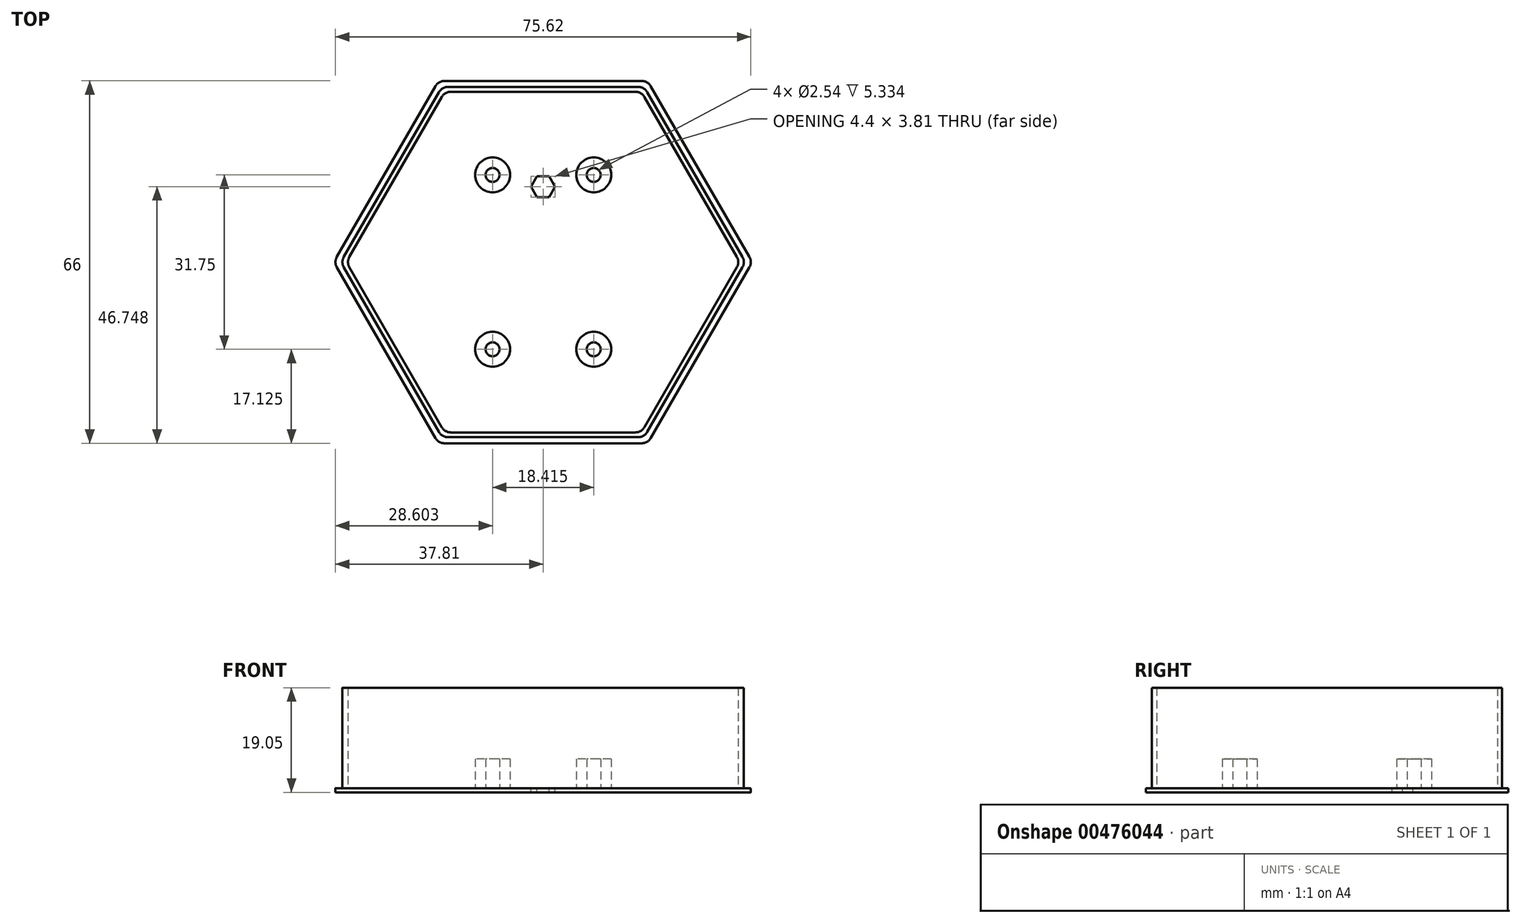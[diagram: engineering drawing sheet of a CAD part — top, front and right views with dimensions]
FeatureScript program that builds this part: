
annotation { "Feature Type Name" : "Feature", "Feature Type Description" : "" }
export const myFeature = defineFeature(function(context is Context, id is Id, definition is map)
    precondition{}
    {
        {
            var Q0;
            Q0=qCreatedBy(makeId("Top.planeOp"),FACE);
            var sketch = newSketch(context, id + "F0", { "sketchPlane" : qUnion([Q0])});
            skLineSegment(sketch, "E0", {"start": v(-56.1, -68.55) * mm, "end": v(58.07, -68.55) * mm});
            skLineSegment(sketch, "E1", {"start": v(0, 0) * mm, "end": v(-19.05, 33) * mm, "construction": true});
            skLineSegment(sketch, "E2", {"start": v(19.05, 33) * mm, "end": v(0, 0) * mm, "construction": true});
            skLineSegment(sketch, "E3", {"start": v(-19.05, 33) * mm, "end": v(19.05, 33) * mm});
            skLineSegment(sketch, "E4.1.0", {"start": v(-38.1, 0) * mm, "end": v(-19.05, 33) * mm});
            skLineSegment(sketch, "E4.2.0", {"start": v(-19.05, -33) * mm, "end": v(-38.1, 0) * mm});
            skLineSegment(sketch, "E4.3.0", {"start": v(19.05, -33) * mm, "end": v(-19.05, -33) * mm});
            skLineSegment(sketch, "E4.4.0", {"start": v(38.1, 0) * mm, "end": v(19.05, -33) * mm});
            skLineSegment(sketch, "E4.5.0", {"start": v(19.05, 33) * mm, "end": v(38.1, 0) * mm});
            skPoint(sketch, "E4.center", {"position": v(0, 0) * mm});
            skSolve(sketch);
        }
        {
            var Q0;
            Q0=makeQuery(id+"F0.imprint","IMPRINT",FACE,{"disambiguationData":[TD([[makeQuery(id+"F0.imprint","IMPRINT",EDGE,{"derivedFrom":sQuery(id+"F0.wireOp",EDGE,"E3")}),-1.0]])]});
            extrude(context, id + "F1", {"entities" : qUnion([Q0]), "depth" : 0.76 * mm, "offsetDistance" : 25.4 * mm});
        }
        {
            var Q0;
            Q0=makeQuery(id+"FdZoSmRdGPEDfu0_1.splitOp","SPLIT",EDGE,{"derivedFrom":makeQuery(id+"F1.opExtrude","SWEPT_EDGE",EDGE,{"disambiguationData":[OSD([sQuery(id+"F0.wireOp",EDGE,"E4.4.0"),sQuery(id+"F0.wireOp",EDGE,"E4.5.0")])]})});
            var Q1;
            Q1=makeQuery(id+"FdZoSmRdGPEDfu0_1.splitOp","SPLIT",EDGE,{"derivedFrom":makeQuery(id+"F1.opExtrude","SWEPT_EDGE",EDGE,{"disambiguationData":[OSD([sQuery(id+"F0.wireOp",EDGE,"E3"),sQuery(id+"F0.wireOp",EDGE,"E4.5.0")])]})});
            var Q2;
            Q2=makeQuery(id+"FdZoSmRdGPEDfu0_1.splitOp","SPLIT",EDGE,{"derivedFrom":makeQuery(id+"F1.opExtrude","SWEPT_EDGE",EDGE,{"disambiguationData":[OSD([sQuery(id+"F0.wireOp",EDGE,"E3"),sQuery(id+"F0.wireOp",EDGE,"E4.1.0")])]})});
            var Q3;
            Q3=makeQuery(id+"FdZoSmRdGPEDfu0_1.splitOp","SPLIT",EDGE,{"derivedFrom":makeQuery(id+"F1.opExtrude","SWEPT_EDGE",EDGE,{"disambiguationData":[OSD([sQuery(id+"F0.wireOp",EDGE,"E4.1.0"),sQuery(id+"F0.wireOp",EDGE,"E4.2.0")])]})});
            var Q4;
            Q4=makeQuery(id+"FdZoSmRdGPEDfu0_1.splitOp","SPLIT",EDGE,{"derivedFrom":makeQuery(id+"F1.opExtrude","SWEPT_EDGE",EDGE,{"disambiguationData":[OSD([sQuery(id+"F0.wireOp",EDGE,"E4.2.0"),sQuery(id+"F0.wireOp",EDGE,"E4.3.0")])]})});
            var Q5;
            Q5=makeQuery(id+"FdZoSmRdGPEDfu0_1.splitOp","SPLIT",EDGE,{"derivedFrom":makeQuery(id+"F1.opExtrude","SWEPT_EDGE",EDGE,{"disambiguationData":[OSD([sQuery(id+"F0.wireOp",EDGE,"E4.3.0"),sQuery(id+"F0.wireOp",EDGE,"E4.4.0")])]})});
            fillet(context, id + "F2", {"entities" : qUnion([Q0, Q1, Q2, Q3, Q4, Q5]), "radius" : 1.9 * mm, "allowEdgeOverflow" : false});
        }
        {
            var Q0;
            Q0=qCreatedBy(makeId("Top.planeOp"),FACE);
            var sketch = newSketch(context, id + "F3", { "sketchPlane" : qUnion([Q0])});
            skLineSegment(sketch, "E5", {"start": v(0, 0) * mm, "end": v(-18.41, 31.9) * mm, "construction": true});
            skLineSegment(sketch, "E6", {"start": v(0, 0) * mm, "end": v(18.41, 31.9) * mm, "construction": true});
            skLineSegment(sketch, "E7", {"start": v(-18.41, 31.9) * mm, "end": v(18.41, 31.9) * mm});
            skLineSegment(sketch, "E8.1.0", {"start": v(-36.83, 0) * mm, "end": v(-18.41, 31.9) * mm});
            skLineSegment(sketch, "E8.2.0", {"start": v(-18.42, -31.9) * mm, "end": v(-36.83, 0) * mm});
            skLineSegment(sketch, "E8.3.0", {"start": v(18.41, -31.9) * mm, "end": v(-18.41, -31.9) * mm});
            skLineSegment(sketch, "E8.4.0", {"start": v(36.83, 0) * mm, "end": v(18.41, -31.9) * mm});
            skLineSegment(sketch, "E8.5.0", {"start": v(18.41, 31.9) * mm, "end": v(36.83, 0) * mm});
            skPoint(sketch, "E8.center", {"position": v(0, 0) * mm});
            skSolve(sketch);
        }
        {
            var Q0;
            Q0=qSketchRegion(id+"F3",true);
            extrude(context, id + "F4", {"entities" : qUnion([Q0]), "depth" : 19.05 * mm, "offsetDistance" : 25.4 * mm});
        }
        {
            var Q0;
            Q0=makeQuery(id+"F4.opExtrude","SWEPT_EDGE",EDGE,{"disambiguationData":[OSD([sQuery(id+"F3.wireOp",EDGE,"E8.2.0"),sQuery(id+"F3.wireOp",EDGE,"E8.3.0")])]});
            var Q1;
            Q1=makeQuery(id+"F4.opExtrude","SWEPT_EDGE",EDGE,{"disambiguationData":[OSD([sQuery(id+"F3.wireOp",EDGE,"E8.3.0"),sQuery(id+"F3.wireOp",EDGE,"E8.4.0")])]});
            var Q2;
            Q2=makeQuery(id+"F4.opExtrude","SWEPT_EDGE",EDGE,{"disambiguationData":[OSD([sQuery(id+"F3.wireOp",EDGE,"E8.4.0"),sQuery(id+"F3.wireOp",EDGE,"E8.5.0")])]});
            var Q3;
            Q3=makeQuery(id+"F4.opExtrude","SWEPT_EDGE",EDGE,{"disambiguationData":[OSD([sQuery(id+"F3.wireOp",EDGE,"E8.1.0"),sQuery(id+"F3.wireOp",EDGE,"E8.2.0")])]});
            var Q4;
            Q4=makeQuery(id+"F4.opExtrude","SWEPT_EDGE",EDGE,{"disambiguationData":[OSD([sQuery(id+"F3.wireOp",EDGE,"E7"),sQuery(id+"F3.wireOp",EDGE,"E8.5.0")])]});
            var Q5;
            Q5=makeQuery(id+"F4.opExtrude","SWEPT_EDGE",EDGE,{"disambiguationData":[OSD([sQuery(id+"F3.wireOp",EDGE,"E7"),sQuery(id+"F3.wireOp",EDGE,"E8.1.0")])]});
            fillet(context, id + "F5", {"entities" : qUnion([Q0, Q1, Q2, Q3, Q4, Q5]), "radius" : 1.9 * mm, "tangentPropagation" : true, "allowEdgeOverflow" : false});
        }
        {
            var Q0;
            Q0=qCreatedBy(makeId("Top.planeOp"),FACE);
            var sketch = newSketch(context, id + "F6", { "sketchPlane" : qUnion([Q0])});
            skLineSegment(sketch, "E9", {"start": v(-17.9, 31.02) * mm, "end": v(0, 0) * mm, "construction": true});
            skLineSegment(sketch, "E10", {"start": v(0, 0) * mm, "end": v(17.9, 31.02) * mm, "construction": true});
            skLineSegment(sketch, "E11", {"start": v(-17.9, 31.02) * mm, "end": v(17.9, 31.02) * mm});
            skLineSegment(sketch, "E12.1.0", {"start": v(-35.81, 0) * mm, "end": v(-17.9, 31.02) * mm});
            skLineSegment(sketch, "E12.2.0", {"start": v(-17.9, -31.02) * mm, "end": v(-35.81, 0) * mm});
            skLineSegment(sketch, "E12.3.0", {"start": v(17.9, -31.02) * mm, "end": v(-17.9, -31.02) * mm});
            skLineSegment(sketch, "E12.4.0", {"start": v(35.81, 0) * mm, "end": v(17.9, -31.02) * mm});
            skLineSegment(sketch, "E12.5.0", {"start": v(17.9, 31.02) * mm, "end": v(35.81, 0) * mm});
            skPoint(sketch, "E12.center", {"position": v(0, 0) * mm});
            skSolve(sketch);
        }
        {
            var Q0;
            Q0 = qSketchRegion(id + "F6", true);
            extrude(context, id + "F7", {"entities" : qUnion([Q0]), "depth" : 25.4 * mm, "offsetDistance" : 25.4 * mm});
        }
        {
            var Q0;
            Q0=makeQuery(id+"F7.opExtrude","SWEPT_EDGE",EDGE,{"disambiguationData":[OSD([sQuery(id+"F6.wireOp",EDGE,"E12.2.0"),sQuery(id+"F6.wireOp",EDGE,"E12.3.0")])]});
            var Q1;
            Q1=makeQuery(id+"F7.opExtrude","SWEPT_EDGE",EDGE,{"disambiguationData":[OSD([sQuery(id+"F6.wireOp",EDGE,"E12.3.0"),sQuery(id+"F6.wireOp",EDGE,"E12.4.0")])]});
            var Q2;
            Q2=makeQuery(id+"F7.opExtrude","SWEPT_EDGE",EDGE,{"disambiguationData":[OSD([sQuery(id+"F6.wireOp",EDGE,"E12.4.0"),sQuery(id+"F6.wireOp",EDGE,"E12.5.0")])]});
            var Q3;
            Q3=makeQuery(id+"F7.opExtrude","SWEPT_EDGE",EDGE,{"disambiguationData":[OSD([sQuery(id+"F6.wireOp",EDGE,"E12.1.0"),sQuery(id+"F6.wireOp",EDGE,"E12.2.0")])]});
            var Q4;
            Q4=makeQuery(id+"F7.opExtrude","SWEPT_EDGE",EDGE,{"disambiguationData":[OSD([sQuery(id+"F6.wireOp",EDGE,"E11"),sQuery(id+"F6.wireOp",EDGE,"E12.5.0")])]});
            var Q5;
            Q5=makeQuery(id+"F7.opExtrude","SWEPT_EDGE",EDGE,{"disambiguationData":[OSD([sQuery(id+"F6.wireOp",EDGE,"E11"),sQuery(id+"F6.wireOp",EDGE,"E12.1.0")])]});
            fillet(context, id + "F8", {"entities" : qUnion([Q0, Q1, Q2, Q3, Q4, Q5]), "radius" : 1.9 * mm, "tangentPropagation" : true, "allowEdgeOverflow" : false});
        }
        {
            var Q0;
            Q0=makeQuery(id+"F7.opExtrude","SWEPT_BODY",BODY,{"disambiguationData":[OSD([sQuery(id+"F6.wireOp",EDGE,"E11"),sQuery(id+"F6.wireOp",EDGE,"E12.1.0"),sQuery(id+"F6.wireOp",EDGE,"E12.2.0"),sQuery(id+"F6.wireOp",EDGE,"E12.3.0"),sQuery(id+"F6.wireOp",EDGE,"E12.4.0"),sQuery(id+"F6.wireOp",EDGE,"E12.5.0")])]});
            transform(context, id + "F9", {"entities" : qUnion([Q0]), "transformType" : TransformType.TRANSLATION_3D, "dx" : 0 * mm, "dy" : 0 * mm, "dz" : 0.76 * mm, "makeCopy" : false});
        }
        {
            var Q0;
            Q0=makeQuery(id+"F7.opExtrude","SWEPT_BODY",BODY,{"disambiguationData":[OSD([sQuery(id+"F6.wireOp",EDGE,"E11"),sQuery(id+"F6.wireOp",EDGE,"E12.1.0"),sQuery(id+"F6.wireOp",EDGE,"E12.2.0"),sQuery(id+"F6.wireOp",EDGE,"E12.3.0"),sQuery(id+"F6.wireOp",EDGE,"E12.4.0"),sQuery(id+"F6.wireOp",EDGE,"E12.5.0")])]});
            var Q1;
            Q1=makeQuery(id+"F4.opExtrude","SWEPT_BODY",BODY,{"disambiguationData":[OSD([sQuery(id+"F3.wireOp",EDGE,"E7"),sQuery(id+"F3.wireOp",EDGE,"E8.1.0"),sQuery(id+"F3.wireOp",EDGE,"E8.2.0"),sQuery(id+"F3.wireOp",EDGE,"E8.3.0"),sQuery(id+"F3.wireOp",EDGE,"E8.4.0"),sQuery(id+"F3.wireOp",EDGE,"E8.5.0")])]});
            booleanBodies(context, id + "F10", {"operationType" : BooleanOperationType.SUBTRACTION, "tools" : qUnion([Q0]), "targets" : qUnion([Q1])});
        }
        {
            var Q0;
            Q0=makeQuery(id+"F10.opBoolean","COPY",FACE,{"derivedFrom":makeQuery(id+"F7.opExtrude","CAP_FACE",FACE,{"disambiguationData":[OSD([sQuery(id+"F6.wireOp",EDGE,"E11"),sQuery(id+"F6.wireOp",EDGE,"E12.1.0"),sQuery(id+"F6.wireOp",EDGE,"E12.2.0"),sQuery(id+"F6.wireOp",EDGE,"E12.3.0"),sQuery(id+"F6.wireOp",EDGE,"E12.4.0"),sQuery(id+"F6.wireOp",EDGE,"E12.5.0")])],"isStart":true})});
            var sketch = newSketch(context, id + "F11", { "sketchPlane" : qUnion([Q0])});
            skLineSegment(sketch, "E13.bottom", {"start": v(-12.7, 19.3) * mm, "end": v(12.7, 19.3) * mm});
            skLineSegment(sketch, "E13.top", {"start": v(-12.7, -19.3) * mm, "end": v(12.7, -19.3) * mm});
            skLineSegment(sketch, "E13.left", {"start": v(-12.7, 19.3) * mm, "end": v(-12.7, -19.3) * mm});
            skLineSegment(sketch, "E13.right", {"start": v(12.7, 19.3) * mm, "end": v(12.7, -19.3) * mm});
            skPoint(sketch, "E14", {"position": v(0, 13.75) * mm});
            skLineSegment(sketch, "E15", {"start": v(-12.7, 0) * mm, "end": v(12.7, 0) * mm, "construction": true});
            skLineSegment(sketch, "E16.bottom", {"start": v(9.2, 15.88) * mm, "end": v(-9.2, 15.88) * mm, "construction": true});
            skLineSegment(sketch, "E16.top", {"start": v(9.2, -15.88) * mm, "end": v(-9.2, -15.88) * mm, "construction": true});
            skLineSegment(sketch, "E16.left", {"start": v(9.2, 15.87) * mm, "end": v(9.2, -15.88) * mm, "construction": true});
            skLineSegment(sketch, "E16.right", {"start": v(-9.2, 15.88) * mm, "end": v(-9.2, -15.88) * mm, "construction": true});
            skCircle(sketch, "E17", {"center": v(-9.2, 15.88) * mm, "radius": 3.18 * mm});
            skCircle(sketch, "E18", {"center": v(9.2, 15.88) * mm, "radius": 3.18 * mm});
            skCircle(sketch, "E19", {"center": v(-9.2, -15.88) * mm, "radius": 3.18 * mm});
            skCircle(sketch, "E20", {"center": v(9.2, -15.88) * mm, "radius": 3.18 * mm});
            skCircle(sketch, "E21", {"center": v(-9.2, 15.88) * mm, "radius": 1.27 * mm});
            skCircle(sketch, "E22", {"center": v(9.2, 15.88) * mm, "radius": 1.27 * mm});
            skCircle(sketch, "E23", {"center": v(-9.2, -15.88) * mm, "radius": 1.27 * mm});
            skCircle(sketch, "E24", {"center": v(9.2, -15.88) * mm, "radius": 1.27 * mm});
            skCircle(sketch, "E25.cCircle", {"center": v(0, 13.75) * mm, "radius": 1.9 * mm, "construction": true});
            skLineSegment(sketch, "E25.0", {"start": v(1.1, 11.84) * mm, "end": v(-1.1, 11.84) * mm});
            skLineSegment(sketch, "E25.1", {"start": v(-1.1, 11.84) * mm, "end": v(-2.2, 13.75) * mm});
            skLineSegment(sketch, "E25.2", {"start": v(-2.2, 13.75) * mm, "end": v(-1.1, 15.65) * mm});
            skLineSegment(sketch, "E25.3", {"start": v(-1.1, 15.65) * mm, "end": v(1.1, 15.65) * mm});
            skLineSegment(sketch, "E25.4", {"start": v(1.1, 15.65) * mm, "end": v(2.2, 13.75) * mm});
            skLineSegment(sketch, "E25.5", {"start": v(2.2, 13.75) * mm, "end": v(1.1, 11.84) * mm});
            skPoint(sketch, "E25.0.midPoint", {"position": v(0, 11.84) * mm});
            skSolve(sketch);
        }
        {
            var Q0;
            Q0=makeQuery(id+"F11.imprint","IMPRINT",FACE,{"disambiguationData":[TD([[makeQuery(id+"F11.imprint","IMPRINT",EDGE,{"derivedFrom":sQuery(id+"F11.wireOp",EDGE,"E17")}),1.0]])]});
            var Q1;
            Q1=makeQuery(id+"F11.imprint","IMPRINT",FACE,{"disambiguationData":[TD([[makeQuery(id+"F11.imprint","IMPRINT",EDGE,{"derivedFrom":sQuery(id+"F11.wireOp",EDGE,"E18")}),1.0]])]});
            var Q2;
            Q2=makeQuery(id+"F11.imprint","IMPRINT",FACE,{"disambiguationData":[TD([[makeQuery(id+"F11.imprint","IMPRINT",EDGE,{"derivedFrom":sQuery(id+"F11.wireOp",EDGE,"E20")}),1.0]])]});
            var Q3;
            Q3=makeQuery(id+"F11.imprint","IMPRINT",FACE,{"disambiguationData":[TD([[makeQuery(id+"F11.imprint","IMPRINT",EDGE,{"derivedFrom":sQuery(id+"F11.wireOp",EDGE,"E19")}),1.0]])]});
            extrude(context, id + "F12", {"entities" : qUnion([Q0, Q1, Q2, Q3]), "operationType" : NewBodyOperationType.ADD, "depth" : 5.33 * mm, "offsetDistance" : 25.4 * mm});
        }
        {
            var Q0;
            Q0=makeQuery(id+"F11.imprint","IMPRINT",FACE,{"disambiguationData":[TD([[makeQuery(id+"F11.imprint","IMPRINT",EDGE,{"derivedFrom":sQuery(id+"F11.wireOp",EDGE,"E25.0")}),-1.0]])]});
            extrude(context, id + "F13", {"entities" : qUnion([Q0]), "operationType" : NewBodyOperationType.REMOVE, "oppositeDirection" : true, "depth" : 2.54 * mm, "offsetDistance" : 25.4 * mm});
        }
    });
